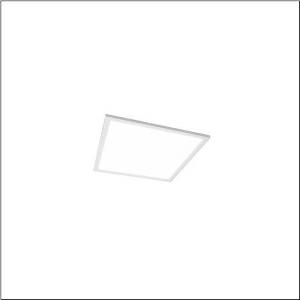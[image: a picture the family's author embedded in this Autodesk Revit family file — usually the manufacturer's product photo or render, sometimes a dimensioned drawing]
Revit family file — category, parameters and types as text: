
# Revit family: apollon_r__21_square_51mq13wd2313_d027
name_source: partatom
category: Lighting Fixtures
units: mm (PartAtom-declared; Revit-internal decimal feet)

## family parameters
Cut with Voids When Loaded = No
Host = Face
Light Source = No
Part Type = Normal
Room Calculation Point = No
Round Connector Dimension = Use Diameter
Shared = No

## types (1)
- Apollon® 21 square (1 x LED, 1700 lm, 15 W, 3000K)
    Apparent Load = 15 VA
    CIE Flux Codes = 59 88 97 100 100
    Color Rendering = 80
    Color Temperature = 3000K
    Default Elevation = 1800 mm
    Description = Apollon® 21 square, office luminaire, primary optical cover: micro prismatic cover, of PMMA, CAT 2 (L<= 3000cd/m²), light emission: direct distribution, primary light characteristic: symmetric, installation type: lay-in mounting, LED, rated luminous flux: 1.700lm, luminous efficacy: 113lm/W, light colour: 830, colour temperature: 3000K, control gear: DALI 2, with terminal, 5-pole, mains connection: 220..240V, AC, 50/60Hz, rated input power: 15W, housing, of sheet steel, coated, pure white, length: 296mm, width: 296mm, height: 40mm, housing upper side, of sheet steel, galvanised, protection rating (complete): IP20, protection rating (lamp compartment, on room side): IP50, insulation class (complete): insulation class II (safety insulation), certification: CE, ENEC, permissible operating ambient temperature: -20..+40°C, packaging unit: 1 piece
    Height = 0 mm  [stored 0 ft]
    Lamp = 1 x LED
    Lamp Light Flux = 1700 lm
    Lamp Power = 15 W
    Lamp count = 1
    Length = 295 mm
    Luminous efficacy = 113 lm/W
    Manufacturer = Siteco
    ModVariant = No
    Model = 51MQ13WD2313
    Mounting Place = Ceiling
    Mounting Type = Recessed
    Number of Poles = 1
    OnlyDefault = Yes
    Power Factor = 1
    Product Name = Apollon® 21 square
    Product group = office luminaire | ceiling recessed
    ProductGroupID = 401
    Protection Class = Protection class II
    Protection Degree = IP 20
    RLX_Detail_Level = 1
    RLX_Emergency_Light_Flux = 0 lm
    RLX_Emergency_Type = 0
    RLX_Emergency_Type_DB = No
    RlxData = <blob elided: 9109 chars, md5=537abf3f>
    Socket = socket
    Standby Power = 0 W
    System Light Flux = 1700 lm
    System Power = 15 W
    Type Comments = Product without accessories
    Type Image = l_1291030.jpg
    URL = http://relux.com
    VarID = ---
    Voltage = 0 V
    Weight = 0.00 kg
    Width = 295 mm

note: [stored X ft] marks values corroborated as IEEE doubles in the binary element streams (Revit-internal decimal feet)

## geometry (parser evidence)
native form markers: Sweep x10
no freeform markers — native parametric forms only
